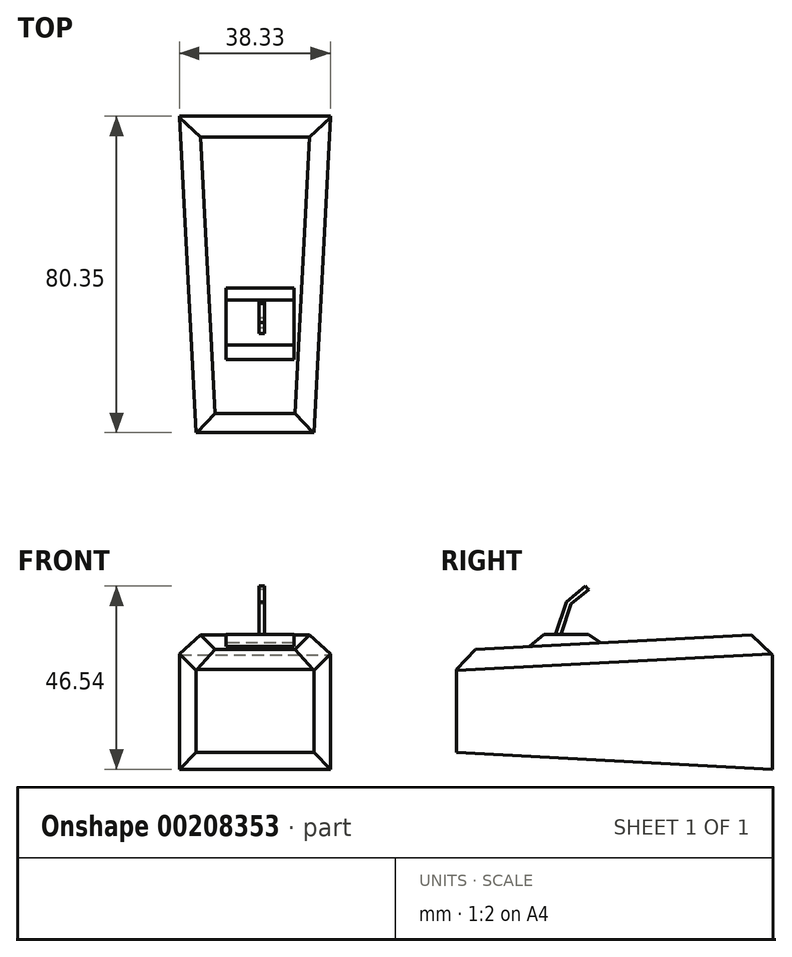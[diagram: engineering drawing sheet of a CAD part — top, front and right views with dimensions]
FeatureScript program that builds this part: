
annotation { "Feature Type Name" : "Feature", "Feature Type Description" : "" }
export const myFeature = defineFeature(function(context is Context, id is Id, definition is map)
    precondition{}
    {
        {
            var Q0;
            Q0=qCreatedBy(makeId("Front.planeOp"),FACE);
            var sketch = newSketch(context, id + "F0", { "sketchPlane" : qUnion([Q0])});
            skLineSegment(sketch, "E0", {"start": v(-15.93, 0) * mm, "end": v(-15.93, -26.01) * mm});
            skLineSegment(sketch, "E1", {"start": v(-15.93, -26.01) * mm, "end": v(13.98, -26.01) * mm});
            skLineSegment(sketch, "E2", {"start": v(13.98, -26.01) * mm, "end": v(13.98, 0) * mm});
            skLineSegment(sketch, "E3", {"start": v(13.98, 0) * mm, "end": v(-15.93, 0) * mm});
            skSolve(sketch);
        }
        {
            var Q0;
            Q0 = qSketchRegion(id + "F0", true);
            extrude(context, id + "F4", {"entities" : qUnion([Q0]), "oppositeDirection" : true, "depth" : 80.35 * mm, "hasDraft" : true, "draftAngle" : 3 * degree});
        }
        {
            var Q0;
            Q0=makeQuery(id+"F4.opExtrude","SWEPT_EDGE",EDGE,{"disambiguationData":[OSD([sQuery(id+"F0.wireOp",EDGE,"E2"),sQuery(id+"F0.wireOp",EDGE,"E3")])]});
            var Q1;
            Q1=makeQuery(id+"F4.opExtrude","SWEPT_FACE",FACE,{"disambiguationData":[OSD([sQuery(id+"F0.wireOp",EDGE,"E3")])]});
            chamfer(context, id + "F5", {"entities" : qUnion([Q0, Q1]), "width" : 5.08 * mm, "tangentPropagation" : true});
        }
        {
            var Q0;
            Q0=qCreatedBy(makeId("Right.planeOp"),FACE);
            var sketch = newSketch(context, id + "F1", { "sketchPlane" : qUnion([Q0])});
            skLineSegment(sketch, "E4", {"start": v(17.45, 0) * mm, "end": v(22.2, 4.08) * mm});
            skLineSegment(sketch, "E5", {"start": v(22.2, 4.08) * mm, "end": v(33.61, 4.08) * mm});
            skLineSegment(sketch, "E6", {"start": v(33.61, 4.08) * mm, "end": v(39.56, 0) * mm});
            skLineSegment(sketch, "E7", {"start": v(39.56, 0) * mm, "end": v(17.45, 0) * mm});
            skLineSegment(sketch, "E8", {"start": v(25.16, 4.08) * mm, "end": v(27.9, 12.25) * mm});
            skPoint(sketch, "E8.endSnap0", {"position": v(27.9, 4.08) * mm});
            skLineSegment(sketch, "E9", {"start": v(27.9, 12.25) * mm, "end": v(34.46, 17.68) * mm});
            skLineSegment(sketch, "E10", {"start": v(26.53, 4.08) * mm, "end": v(29.12, 11.76) * mm});
            skPoint(sketch, "E10.startSnap0", {"position": v(26.53, 8.16) * mm});
            skLineSegment(sketch, "E11", {"start": v(29.12, 11.76) * mm, "end": v(29.12, 11.76) * mm});
            skLineSegment(sketch, "E12", {"start": v(29.12, 11.76) * mm, "end": v(35.14, 16.75) * mm});
            skCircle(sketch, "E13", {"center": v(34.7, 17.31) * mm, "radius": 2.11 * mm});
            skSolve(sketch);
        }
        {
            var Q0;
            {var subQ3=sQuery(id+"F1.wireOp",EDGE,"E4");Q0=makeQuery(id+"F1.imprint","IMPRINT",FACE,{"disambiguationData":[TD([[makeQuery(id+"F1.imprint","IMPRINT",EDGE,{"derivedFrom":subQ3}),-1.0]])]});}
            extrude(context, id + "F6", {"entities" : qUnion([Q0]), "operationType" : NewBodyOperationType.ADD, "depth" : 8.9 * mm});
        }
        {
            var Q0;
            Q0=makeQuery(id+"F6.opExtrude","CAP_FACE",FACE,{"disambiguationData":[OSD([sQuery(id+"F1.wireOp",EDGE,"E4"),sQuery(id+"F1.wireOp",EDGE,"E5"),sQuery(id+"F1.wireOp",EDGE,"E6"),sQuery(id+"F1.wireOp",EDGE,"E7")])],"isStart":true});
            extrude(context, id + "F7", {"entities" : qUnion([Q0]), "operationType" : NewBodyOperationType.ADD, "depth" : 8.36 * mm});
        }
        {
            var Q0;
            {var subQ2=sQuery(id+"F1.wireOp",EDGE,"E8");Q0=makeQuery(id+"F1.imprint","IMPRINT",FACE,{"disambiguationData":[TD([[makeQuery(id+"F1.imprint","IMPRINT",EDGE,{"derivedFrom":subQ2}),-1.0]])]});}
            extrude(context, id + "F2", {"entities" : qUnion([Q0]), "operationType" : NewBodyOperationType.ADD, "depth" : 1.47 * mm});
        }
        {
            var Q0;
            Q0=sQuery(id+"F1.wireOp",EDGE,"E13");
            extrude(context, id + "F3", {"bodyType" : ToolBodyType.SURFACE, "surfaceEntities" : qUnion([Q0]), "depth" : 1.76 * mm});
        }
    });
